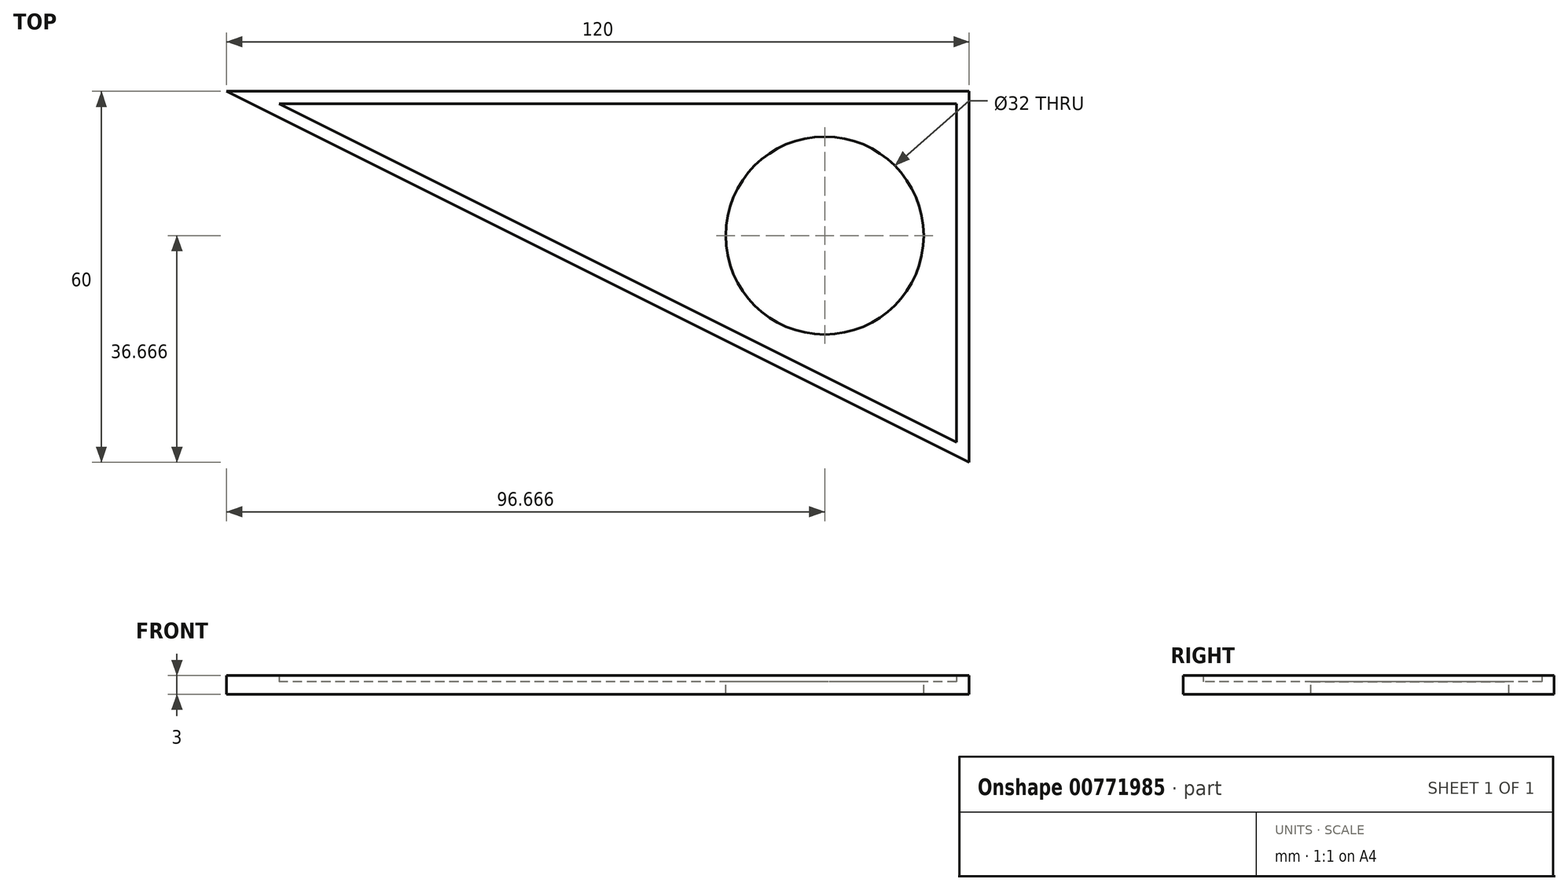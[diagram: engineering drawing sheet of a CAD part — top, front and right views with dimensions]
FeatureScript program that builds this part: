
annotation { "Feature Type Name" : "Feature", "Feature Type Description" : "" }
export const myFeature = defineFeature(function(context is Context, id is Id, definition is map)
    precondition{}
    {
        {
            var Q0;
            Q0=qCreatedBy(makeId("Top.planeOp"),FACE);
            var sketch = newSketch(context, id + "F0", { "sketchPlane" : qUnion([Q0])});
            skLineSegment(sketch, "E0", {"start": v(0, 0) * mm, "end": v(-120, 0) * mm});
            skLineSegment(sketch, "E1", {"start": v(0, 0) * mm, "end": v(0, -60) * mm});
            skLineSegment(sketch, "E2", {"start": v(-120, 0) * mm, "end": v(0, -60) * mm});
            skSolve(sketch);
        }
        {
            var Q0;
            Q0 = qSketchRegion(id + "F0", true);
            extrude(context, id + "F1", {"entities" : qUnion([Q0]), "depth" : 3 * mm, "offsetDistance" : 25 * mm});
        }
        {
            var Q0;
            Q0=makeQuery(id+"F1.opExtrude","CAP_FACE",FACE,{"disambiguationData":[OSD([sQuery(id+"F0.wireOp",EDGE,"E0"),sQuery(id+"F0.wireOp",EDGE,"E1"),sQuery(id+"F0.wireOp",EDGE,"E2")])],"isStart":false});
            shell(context, id + "F2", {"entities" : qUnion([Q0]), "thickness" : 2 * mm});
        }
        {
            var Q0;
            Q0=makeQuery(id+"F2.opShell","OFFSET_FACE",FACE,{"disambiguationData":[OSD([sQuery(id+"F0.wireOp",EDGE,"E0"),sQuery(id+"F0.wireOp",EDGE,"E1"),sQuery(id+"F0.wireOp",EDGE,"E2")])]});
            var sketch = newSketch(context, id + "F3", { "sketchPlane" : qUnion([Q0])});
            skPoint(sketch, "E3", {"position": v(-23.33, -23.33) * mm});
            skLineSegment(sketch, "E4", {"start": v(0, 0) * mm, "end": v(-23.33, -23.33) * mm});
            skCircle(sketch, "E5", {"center": v(-23.33, -23.33) * mm, "radius": 16 * mm});
            skSolve(sketch);
        }
        {
            var Q0;
            Q0 = qSketchRegion(id + "F3", true);
            extrude(context, id + "F4", {"entities" : qUnion([Q0]), "operationType" : NewBodyOperationType.REMOVE, "endBound" : BoundingType.THROUGH_ALL, "oppositeDirection" : true, "depth" : 25 * mm, "offsetDistance" : 25 * mm});
        }
    });
